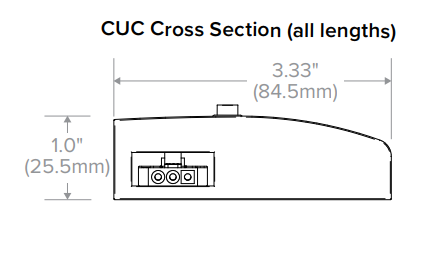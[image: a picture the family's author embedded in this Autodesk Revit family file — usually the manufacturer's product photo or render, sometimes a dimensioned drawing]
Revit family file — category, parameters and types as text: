
# Revit family: RLB4
name_source: partatom
category: Lighting Fixtures
units: mm (PartAtom-declared; Revit-internal decimal feet)

## family parameters
Cut with Voids When Loaded = No
Host = Face
Light Source = Yes
OmniClass Number = 23.80.70.11.14.17
OmniClass Title = Direct/Indirect
Part Type = Normal
Room Calculation Point = No
Round Connector Dimension = Use Diameter
Shared = Yes

## types (1)
- RLB4
    Apparent Load = 64 VA
    Application = Automotive,Education,Offices,Retail,Government
    Assembly Code = D5020200
    Certifications = All luminaires are built to UL 1598 standards, and bear
appropriate ETL damp location labels.
    Color Filter = 16777215
    Connector Description = Lighting Connector
    Default Elevation = 48 "
    Description = Reverie™ Decorative Low Bay
    Dimming Lamp Color Temperature Shift = <None>
    Dimming Protocol = 0-10V,Step Dimming,Dim-to-Dark
    Emit Shape Visible in Rendering = No
    Emit from Rectangle Length = 47 "
    Emit from Rectangle Width = 5 "
    Features = Optional photometric distributions
• Available in 4' and 8'
• Optional integral emergency battery pack
• Uninterrupted ribbon of light for single or row mount applications
• Optional SpectraSync™ offers two modes of tunable white solutions and integrates seamlessly into a
variety of control systems
• NX Distributed Intelligence™ provides options for standalone and networked integrated sensor with wired
or wireless connectivity for NX system deployments
• Five year warranty
    Housing Material = Paint -  Matte White
    Lamp = LED
    Length = 48 "
    Load Classification = Lighting
    Manufacturer = Columbia Lighting
    Model = RLB4
    Photometric Note = For more ies file please find the above Photometric Web Link
    Photometric Web File = RLB4-30LH-FAA-EDU.ies
    Power Factor = 1
    Reflector Finish = White Glass
    Tilt Angle = -90.00°
    URL = https://www.currentlighting.com
    Voltage = 120 V
    Warranty = 5 years Warranty
    Wattage Comments = Variable Intensity technology provides specifiable lumen output/wattage
    Watts = 64 W
    Width = 8.4 "
    Width 1 = 5 "

## geometry (parser evidence)
native form markers: Blend x19, Sweep x5
no freeform markers — native parametric forms only
